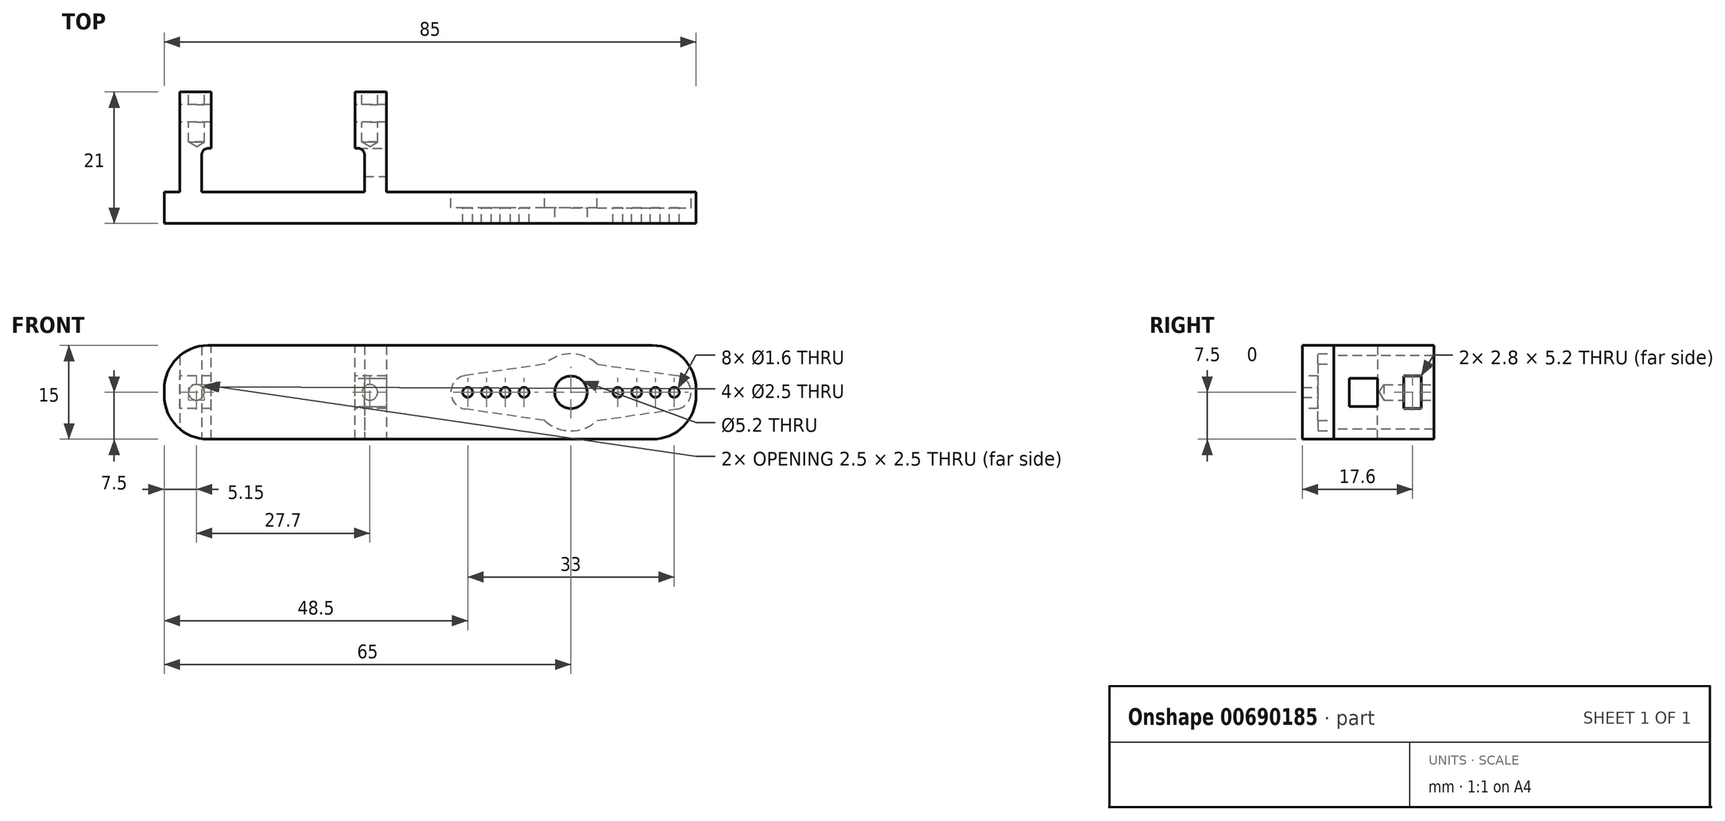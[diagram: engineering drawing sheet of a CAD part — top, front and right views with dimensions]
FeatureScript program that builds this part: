
annotation { "Feature Type Name" : "Feature", "Feature Type Description" : "" }
export const myFeature = defineFeature(function(context is Context, id is Id, definition is map)
    precondition{}
    {
        {
            var Q0;
            Q0=qCreatedBy(makeId("Front.planeOp"),FACE);
            var sketch = newSketch(context, id + "F0", { "sketchPlane" : qUnion([Q0])});
            skLineSegment(sketch, "E0.bottom", {"start": v(0, 7.5) * mm, "end": v(85, 7.5) * mm});
            skLineSegment(sketch, "E0.top", {"start": v(0, -7.5) * mm, "end": v(85, -7.5) * mm});
            skLineSegment(sketch, "E0.left", {"start": v(0, 7.5) * mm, "end": v(0, -7.5) * mm});
            skLineSegment(sketch, "E0.right", {"start": v(85, 7.5) * mm, "end": v(85, -7.5) * mm});
            skPoint(sketch, "E0.middle", {"position": v(42.5, 0) * mm});
            skCircle(sketch, "E1", {"center": v(65, 0) * mm, "radius": 2.6 * mm});
            skSolve(sketch);
        }
        {
            var Q0;
            Q0=makeQuery(id+"F0.imprint","IMPRINT",FACE,{"disambiguationData":[TD([[makeQuery(id+"F0.imprint","IMPRINT",EDGE,{"derivedFrom":sQuery(id+"F0.wireOp",EDGE,"E0.bottom")}),-1.0]])]});
            extrude(context, id + "F1", {"entities" : qUnion([Q0]), "oppositeDirection" : true, "depth" : 5 * mm, "offsetDistance" : 25 * mm});
        }
        {
            var Q0;
            {var subQ1=sQuery(id+"FelzQ8irgmPJCEx_0.wireOp",EDGE,"nqU3fDqP-7IzM-8UvB-soxe-GbgdAJMVhA7a");var subQ3=sQuery(id+"FelzQ8irgmPJCEx_0.wireOp",EDGE,"Wf30qy7B-L3EY-ubdY-4ofm-RBPNTBmtIuBS");var subQ4=sQuery(id+"FelzQ8irgmPJCEx_0.wireOp",EDGE,"0P1yvjZw-iLbS-eAF6-OBv0-oRI93wy17Ioi");var subQ5=sQuery(id+"FelzQ8irgmPJCEx_0.wireOp",EDGE,"IxcgXgfj-hqSl-lfnA-CyWF-p1c6ZB3lQplE");var subQ6=sQuery(id+"FelzQ8irgmPJCEx_0.wireOp",EDGE,"m4ObQz0p-uqgI-Xgwy-2KGq-14yM282HVRsK");var subQ11=makeQuery(id+"FwwyKOTNBZ8lxIx_1.opExtrude","SWEPT_FACE",FACE,{"disambiguationData":[OSD([sQuery(id+"FWpOroBoYfux5cT_1.wireOp",EDGE,"6cmiH4eE-dqzF-GbjJ-dGX1-cgJiLYN27mcO.top")])]});Q0=makeQuery(id+"F1.boolean.opBoolean","MERGE",FACE,{"derivedFrom":[makeQuery(id+"F8gD7zZAfkwsQIA_2.opBoolean","SPLIT",FACE,{"disambiguationData":[TD([makeQuery(id+"FFOvh7GgsPYjLSs_0.opExtrude","CAP_FACE",FACE,{"disambiguationData":[OSD([subQ6,subQ5,subQ4,subQ3,subQ1])],"isStart":true})])],"derivedFrom":subQ11}),makeQuery(id+"F8gD7zZAfkwsQIA_2.opBoolean","SPLIT",FACE,{"disambiguationData":[TD([makeQuery(id+"FwCsV6hsPOMot3H_1.1.FFOvh7GgsPYjLSs_0.opExtrude","CAP_FACE",FACE,{"disambiguationData":[OSD([subQ6,subQ5,subQ4,subQ3,subQ1])],"isStart":true})])],"derivedFrom":subQ11}),makeQuery(id+"F1.opExtrude","CAP_FACE",FACE,{"disambiguationData":[OSD([sQuery(id+"F0.wireOp",EDGE,"E0.bottom"),sQuery(id+"F0.wireOp",EDGE,"E0.top"),sQuery(id+"F0.wireOp",EDGE,"E0.left"),sQuery(id+"F0.wireOp",EDGE,"E0.right"),sQuery(id+"F0.wireOp",EDGE,"E1")])],"isStart":false})]});}
            var sketch = newSketch(context, id + "F2", { "sketchPlane" : qUnion([Q0])});
            skArc(sketch, "E2", {"start": v(-69.2, -4.5) * mm, "mid": v(-65, -6.15) * mm, "end": v(-60.8, -4.5) * mm});
            skLineSegment(sketch, "E3", {"start": v(-65, 6.15) * mm, "end": v(-65, -6.15) * mm, "construction": true});
            skLineSegment(sketch, "E4", {"start": v(-60.8, 4.5) * mm, "end": v(-48.12, 2.67) * mm});
            skLineSegment(sketch, "E5.MirrorCS", {"start": v(-60.8, -4.5) * mm, "end": v(-48.12, -2.67) * mm});
            skLineSegment(sketch, "E6.MirrorCS", {"start": v(-69.2, 4.5) * mm, "end": v(-81.88, 2.67) * mm});
            skLineSegment(sketch, "E7.MirrorCS", {"start": v(-69.2, -4.5) * mm, "end": v(-81.88, -2.67) * mm});
            skArc(sketch, "E8", {"start": v(-48.12, -2.67) * mm, "mid": v(-45.8, 0) * mm, "end": v(-48.12, 2.67) * mm});
            skArc(sketch, "E9.MirrorCS", {"start": v(-81.88, -2.67) * mm, "mid": v(-84.2, 0) * mm, "end": v(-81.88, 2.67) * mm});
            skArc(sketch, "E10.trimOffspring", {"start": v(-60.8, 4.5) * mm, "mid": v(-65, 6.15) * mm, "end": v(-69.2, 4.5) * mm});
            skSolve(sketch);
        }
        {
            var Q0;
            Q0 = qSketchRegion(id + "F2", true);
            extrude(context, id + "F3", {"entities" : qUnion([Q0]), "operationType" : NewBodyOperationType.REMOVE, "oppositeDirection" : true, "depth" : 2.5 * mm, "offsetDistance" : 25 * mm});
        }
        {
            var Q0;
            Q0=makeQuery(id+"F1.opExtrude","SWEPT_EDGE",EDGE,{"disambiguationData":[OSD([sQuery(id+"F0.wireOp",EDGE,"E0.bottom"),sQuery(id+"F0.wireOp",EDGE,"E0.right")])]});
            var Q1;
            Q1=makeQuery(id+"F1.opExtrude","SWEPT_EDGE",EDGE,{"disambiguationData":[OSD([sQuery(id+"F0.wireOp",EDGE,"E0.top"),sQuery(id+"F0.wireOp",EDGE,"E0.right")])]});
            var Q2;
            Q2=makeQuery(id+"F1.opExtrude","SWEPT_EDGE",EDGE,{"disambiguationData":[OSD([sQuery(id+"F0.wireOp",EDGE,"E0.bottom"),sQuery(id+"F0.wireOp",EDGE,"E0.left")])]});
            var Q3;
            Q3=makeQuery(id+"F1.opExtrude","SWEPT_EDGE",EDGE,{"disambiguationData":[OSD([sQuery(id+"F0.wireOp",EDGE,"E0.top"),sQuery(id+"F0.wireOp",EDGE,"E0.left")])]});
            fillet(context, id + "F4", {"entities" : qUnion([Q0, Q1, Q2, Q3]), "radius" : 7 * mm, "tangentPropagation" : true, "allowEdgeOverflow" : false});
        }
        {
            var Q0;
            Q0=makeQuery(id+"F3.boolean.opBoolean","COPY",FACE,{"derivedFrom":makeQuery(id+"F3.opExtrude","CAP_FACE",FACE,{"disambiguationData":[OSD([sQuery(id+"F2.wireOp",EDGE,"E2"),sQuery(id+"F2.wireOp",EDGE,"E4"),sQuery(id+"F2.wireOp",EDGE,"E5.MirrorCS"),sQuery(id+"F2.wireOp",EDGE,"E6.MirrorCS"),sQuery(id+"F2.wireOp",EDGE,"E7.MirrorCS"),sQuery(id+"F2.wireOp",EDGE,"E8"),sQuery(id+"F2.wireOp",EDGE,"E9.MirrorCS"),sQuery(id+"F2.wireOp",EDGE,"E10.trimOffspring")])],"isStart":false})});
            var sketch = newSketch(context, id + "F5", { "sketchPlane" : qUnion([Q0])});
            skCircle(sketch, "E11", {"center": v(-81.5, 0) * mm, "radius": 0.8 * mm});
            skCircle(sketch, "E12", {"center": v(-78.5, 0) * mm, "radius": 0.8 * mm});
            skCircle(sketch, "E13", {"center": v(-75.5, 0) * mm, "radius": 0.8 * mm});
            skCircle(sketch, "E14", {"center": v(-72.5, 0) * mm, "radius": 0.8 * mm});
            skCircle(sketch, "E15", {"center": v(-57.5, 0) * mm, "radius": 0.8 * mm});
            skCircle(sketch, "E16", {"center": v(-54.5, 0) * mm, "radius": 0.8 * mm});
            skCircle(sketch, "E17", {"center": v(-51.5, 0) * mm, "radius": 0.8 * mm});
            skCircle(sketch, "E18", {"center": v(-48.5, 0) * mm, "radius": 0.8 * mm});
            skSolve(sketch);
        }
        {
            var Q0;
            Q0 = qSketchRegion(id + "F5", true);
            extrude(context, id + "F6", {"entities" : qUnion([Q0]), "operationType" : NewBodyOperationType.REMOVE, "endBound" : BoundingType.UP_TO_NEXT, "oppositeDirection" : true, "depth" : 25 * mm, "offsetDistance" : 25 * mm});
        }
        {
            var Q0;
            Q0=makeQuery(id+"F1.opExtrude","CAP_FACE",FACE,{"disambiguationData":[OSD([sQuery(id+"F0.wireOp",EDGE,"E0.bottom"),sQuery(id+"F0.wireOp",EDGE,"E0.top"),sQuery(id+"F0.wireOp",EDGE,"E0.left"),sQuery(id+"F0.wireOp",EDGE,"E0.right"),sQuery(id+"F0.wireOp",EDGE,"E1")])],"isStart":false});
            var sketch = newSketch(context, id + "F7", { "sketchPlane" : qUnion([Q0])});
            skLineSegment(sketch, "E19.bottom", {"start": v(-35.5, 7.5) * mm, "end": v(-30.5, 7.5) * mm});
            skLineSegment(sketch, "E19.top", {"start": v(-35.5, -7.5) * mm, "end": v(-30.5, -7.5) * mm});
            skLineSegment(sketch, "E19.left", {"start": v(-35.5, 7.5) * mm, "end": v(-35.5, -7.5) * mm});
            skLineSegment(sketch, "E19.right", {"start": v(-30.5, 7.5) * mm, "end": v(-30.5, -7.5) * mm});
            skLineSegment(sketch, "E20.bottom", {"start": v(-7.5, 7.5) * mm, "end": v(-7, 7.5) * mm});
            skLineSegment(sketch, "E20.top", {"start": v(-7.5, -7.5) * mm, "end": v(-7, -7.5) * mm});
            skLineSegment(sketch, "E20.left", {"start": v(-7.5, 7.5) * mm, "end": v(-7.5, -7.5) * mm});
            skLineSegment(sketch, "E20.right", {"start": v(-2.5, 5.86) * mm, "end": v(-2.5, -5.86) * mm});
            skLineSegment(sketch, "E21", {"start": v(-19, 14.37) * mm, "end": v(-19, -13.73) * mm, "construction": true});
            skPoint(sketch, "E22", {"position": v(-32.85, 0) * mm});
            skPoint(sketch, "E23", {"position": v(-5.15, 0) * mm});
            skArc(sketch, "E24.0", {"start": v(0, 0.5) * mm, "mid": v(-2.05, 5.45) * mm, "end": v(-7, 7.5) * mm});
            skArc(sketch, "E25.0", {"start": v(-7, -7.5) * mm, "mid": v(-2.05, -5.45) * mm, "end": v(0, -0.5) * mm});
            skSolve(sketch);
        }
        {
            var Q0;
            Q0=makeQuery(id+"F7.imprint","IMPRINT",FACE,{"disambiguationData":[TD([[makeQuery(id+"F7.imprint","IMPRINT",EDGE,{"derivedFrom":sQuery(id+"F7.wireOp",EDGE,"E19.bottom")}),1.0]])]});
            var Q1;
            {var subQ2=sQuery(id+"F7.wireOp",EDGE,"E20.bottom");Q1=makeQuery(id+"F7.imprint","IMPRINT",FACE,{"disambiguationData":[TD([[makeQuery(id+"F7.imprint","IMPRINT",EDGE,{"derivedFrom":subQ2}),1.0]])]});}
            extrude(context, id + "F8", {"entities" : qUnion([Q0, Q1]), "operationType" : NewBodyOperationType.ADD, "depth" : 16 * mm, "offsetDistance" : 25 * mm});
        }
        {
            var Q0;
            Q0=makeQuery(id+"F8.opExtrude","CAP_FACE",FACE,{"disambiguationData":[OSD([sQuery(id+"F7.wireOp",EDGE,"E19.bottom"),sQuery(id+"F7.wireOp",EDGE,"E19.top"),sQuery(id+"F7.wireOp",EDGE,"E19.left"),sQuery(id+"F7.wireOp",EDGE,"E19.right")])],"isStart":false});
            var sketch = newSketch(context, id + "F9", { "sketchPlane" : qUnion([Q0])});
            skPoint(sketch, "E26.0", {"position": v(-32.85, 0) * mm});
            skPoint(sketch, "E27.0", {"position": v(-5.15, 0) * mm});
            skSolve(sketch);
        }
        {
            var Q0;
            Q0=sQuery(id+"F9.wireOp",VERTEX,"E26.0");
            var Q1;
            Q1=sQuery(id+"F9.wireOp",VERTEX,"E27.0");
            var Q2;
            Q2=makeQuery(id+"F1.opExtrude","SWEPT_BODY",BODY,{"disambiguationData":[OSD([sQuery(id+"F0.wireOp",EDGE,"E0.bottom"),sQuery(id+"F0.wireOp",EDGE,"E0.top"),sQuery(id+"F0.wireOp",EDGE,"E0.left"),sQuery(id+"F0.wireOp",EDGE,"E0.right"),sQuery(id+"F0.wireOp",EDGE,"E1")])]});
            hole(context, id + "F10", {"style" : HoleStyle.SIMPLE, "endStyle" : HoleEndStyle.BLIND, "holeDiameter" : 2.5 * mm, "majorDiameter" : 5 * mm, "holeDepth" : 8 * mm, "isTappedThrough" : true, "tappedDepth" : 2.3 * mm, "tapClearance" : 3, "startFromSketch" : true, "locations" : qUnion([Q0, Q1]), "scope" : qUnion([Q2])});
        }
        {
            var Q0;
            Q0=makeQuery(id+"F8.opExtrude","SWEPT_FACE",FACE,{"disambiguationData":[OSD([sQuery(id+"F7.wireOp",EDGE,"E20.right")])]});
            var sketch = newSketch(context, id + "F11", { "sketchPlane" : qUnion([Q0])});
            skLineSegment(sketch, "E28.bottom", {"start": v(-19, -2.6) * mm, "end": v(-16.2, -2.6) * mm});
            skLineSegment(sketch, "E28.top", {"start": v(-19, 2.6) * mm, "end": v(-16.2, 2.6) * mm});
            skLineSegment(sketch, "E28.left", {"start": v(-19, -2.6) * mm, "end": v(-19, 2.6) * mm});
            skLineSegment(sketch, "E28.right", {"start": v(-16.2, -2.6) * mm, "end": v(-16.2, 2.6) * mm});
            skPoint(sketch, "E28.middle", {"position": v(-17.6, 0) * mm});
            skSolve(sketch);
        }
        {
            var Q0;
            Q0=makeQuery(id+"F11.imprint","IMPRINT",FACE,{"disambiguationData":[TD([[makeQuery(id+"F11.imprint","IMPRINT",EDGE,{"derivedFrom":sQuery(id+"F11.wireOp",EDGE,"E28.bottom")}),1.0]])]});
            var Q1;
            Q1=makeQuery(id+"F8.opExtrude","SWEPT_FACE",FACE,{"disambiguationData":[OSD([sQuery(id+"F7.wireOp",EDGE,"E19.left")])]});
            extrude(context, id + "F12", {"entities" : qUnion([Q0]), "operationType" : NewBodyOperationType.REMOVE, "endBound" : BoundingType.UP_TO_SURFACE, "oppositeDirection" : true, "depth" : 25 * mm, "endBoundEntityFace" : qUnion([Q1]), "offsetDistance" : 25 * mm});
        }
        {
            var Q0;
            Q0=makeQuery(id+"F8.boolean.opBoolean","MERGE",FACE,{"derivedFrom":[makeQuery(id+"F1.opExtrude","SWEPT_FACE",FACE,{"disambiguationData":[OSD([sQuery(id+"F0.wireOp",EDGE,"E0.top")])]}),makeQuery(id+"F8.opExtrude","SWEPT_FACE",FACE,{"disambiguationData":[OSD([sQuery(id+"F7.wireOp",EDGE,"E19.top")])]}),makeQuery(id+"F8.opExtrude","SWEPT_FACE",FACE,{"disambiguationData":[OSD([sQuery(id+"F7.wireOp",EDGE,"E20.top")])]})]});
            var sketch = newSketch(context, id + "F13", { "sketchPlane" : qUnion([Q0])});
            skLineSegment(sketch, "E29.bottom", {"start": v(32, -5) * mm, "end": v(6, -5) * mm});
            skLineSegment(sketch, "E29.top", {"start": v(32, -12) * mm, "end": v(6, -12) * mm});
            skLineSegment(sketch, "E29.left", {"start": v(32, -5) * mm, "end": v(32, -12) * mm});
            skLineSegment(sketch, "E29.right", {"start": v(6, -5) * mm, "end": v(6, -12) * mm});
            skPoint(sketch, "E29.middle", {"position": v(19, -8.5) * mm});
            skSolve(sketch);
        }
        {
            var Q0;
            Q0 = qSketchRegion(id + "F13", true);
            var Q1;
            Q1=makeQuery(id+"F8.boolean.opBoolean","MERGE",FACE,{"derivedFrom":[makeQuery(id+"F1.opExtrude","SWEPT_FACE",FACE,{"disambiguationData":[OSD([sQuery(id+"F0.wireOp",EDGE,"E0.bottom")])]}),makeQuery(id+"F8.opExtrude","SWEPT_FACE",FACE,{"disambiguationData":[OSD([sQuery(id+"F7.wireOp",EDGE,"E19.bottom")])]}),makeQuery(id+"F8.opExtrude","SWEPT_FACE",FACE,{"disambiguationData":[OSD([sQuery(id+"F7.wireOp",EDGE,"E20.bottom")])]})]});
            extrude(context, id + "F14", {"entities" : qUnion([Q0]), "operationType" : NewBodyOperationType.REMOVE, "endBound" : BoundingType.UP_TO_SURFACE, "oppositeDirection" : true, "depth" : 25 * mm, "endBoundEntityFace" : qUnion([Q1]), "offsetDistance" : 25 * mm});
        }
        {
            var Q0;
            Q0=makeQuery(id+"F14.boolean.opBoolean","COPY",EDGE,{"derivedFrom":makeQuery(id+"F14.opExtrude","SWEPT_EDGE",EDGE,{"disambiguationData":[OSD([sQuery(id+"F13.wireOp",EDGE,"E29.top"),sQuery(id+"F13.wireOp",EDGE,"E29.left")])]})});
            var Q1;
            Q1=makeQuery(id+"F14.boolean.opBoolean","COPY",EDGE,{"derivedFrom":makeQuery(id+"F14.opExtrude","SWEPT_EDGE",EDGE,{"disambiguationData":[OSD([sQuery(id+"F13.wireOp",EDGE,"E29.top"),sQuery(id+"F13.wireOp",EDGE,"E29.right")])]})});
            fillet(context, id + "F15", {"entities" : qUnion([Q0, Q1]), "radius" : 1 * mm, "tangentPropagation" : true, "allowEdgeOverflow" : false});
        }
        {
            var Q0;
            Q0=makeQuery(id+"F8.opExtrude","SWEPT_FACE",FACE,{"disambiguationData":[OSD([sQuery(id+"F7.wireOp",EDGE,"E19.left")])]});
            var sketch = newSketch(context, id + "F16", { "sketchPlane" : qUnion([Q0])});
            skLineSegment(sketch, "E30.bottom", {"start": v(7.5, 2.25) * mm, "end": v(12, 2.25) * mm});
            skLineSegment(sketch, "E30.top", {"start": v(7.5, -2.25) * mm, "end": v(12, -2.25) * mm});
            skLineSegment(sketch, "E30.left", {"start": v(7.5, 2.25) * mm, "end": v(7.5, -2.25) * mm});
            skLineSegment(sketch, "E30.right", {"start": v(12, 2.25) * mm, "end": v(12, -2.25) * mm});
            skPoint(sketch, "E30.middle", {"position": v(9.75, 0) * mm});
            skSolve(sketch);
        }
        {
            var Q0;
            Q0=makeQuery(id+"F16.imprint","IMPRINT",FACE,{"disambiguationData":[TD([[makeQuery(id+"F16.imprint","IMPRINT",EDGE,{"derivedFrom":sQuery(id+"F16.wireOp",EDGE,"E30.bottom")}),-1.0]])]});
            var Q1;
            Q1=makeQuery(id+"F8.opExtrude","SWEPT_FACE",FACE,{"disambiguationData":[OSD([sQuery(id+"F7.wireOp",EDGE,"E19.right")])]});
            extrude(context, id + "F17", {"entities" : qUnion([Q0]), "operationType" : NewBodyOperationType.REMOVE, "endBound" : BoundingType.UP_TO_SURFACE, "oppositeDirection" : true, "depth" : 25 * mm, "endBoundEntityFace" : qUnion([Q1]), "offsetDistance" : 25 * mm});
        }
    });
